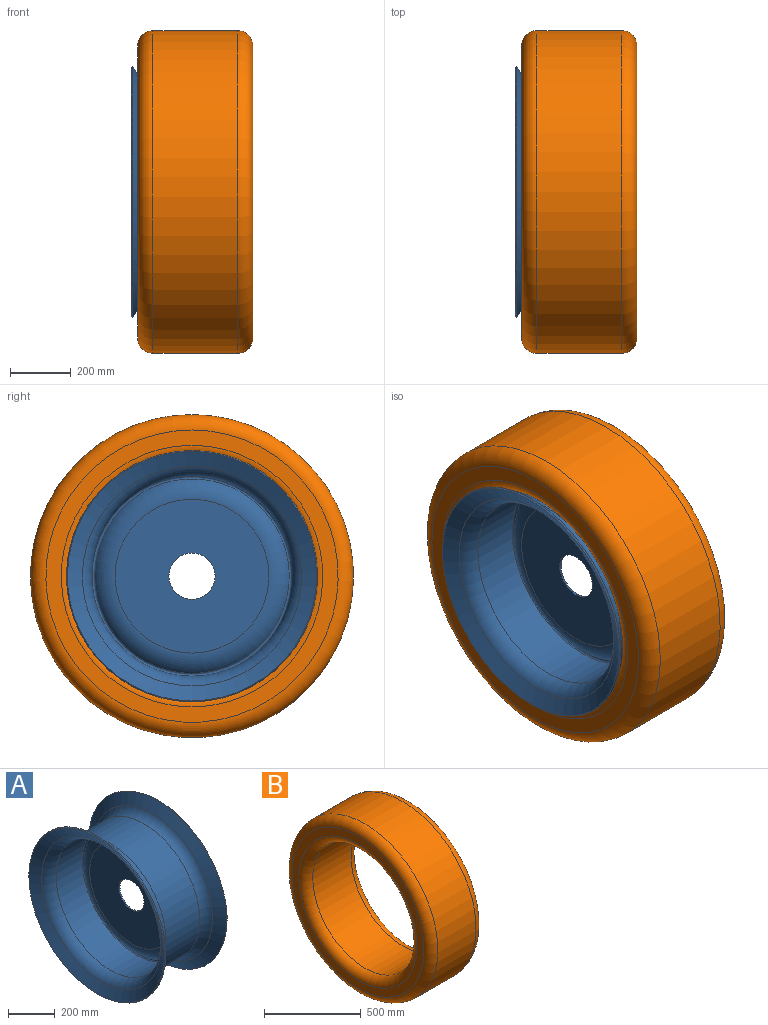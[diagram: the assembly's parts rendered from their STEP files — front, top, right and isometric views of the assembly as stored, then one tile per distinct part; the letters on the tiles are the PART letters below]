
ASSEMBLY  parts=2 mates=1
PART A: 19 faces, bbox 376.3x852.3x852.3 mm
  f0: cone r=416.69mm half-angle=30deg, axis (-1,0,0), area 16688.6mm2, adj f6,f11
  f1: cone r=411.48mm half-angle=30deg, axis (1,0,0), area 16480.7mm2, adj f2,f7
  f2: cone r=365.12mm half-angle=60deg, axis (-1,0,0), area 140106.9mm2, adj f1,f3
  f3: torus R=393.7mm, axis (1,0,0), area 130271.5mm2, adj f2,f4
  f4: cylinder r=336.55mm len=673.1mm, axis (1,0,0), area 435770.6mm2, adj f3,f5
  f5: torus R=393.7mm, axis (1,0,0), area 130271.5mm2, adj f4,f6
  f6: cone r=419.87mm half-angle=60deg, axis (1,0,0), area 155881.4mm2, adj f0,f5
  f7: cone r=361.95mm half-angle=60deg, axis (-1,0,0), area 138966mm2, adj f1,f8
  f8: torus R=393.7mm, axis (1,0,0), area 142552mm2, adj f7,f9
  f9: cylinder r=330.2mm len=660.4mm, axis (1,0,0), area 331161.5mm2, adj f8,f18
  f10: torus R=393.7mm, axis (1,0,0), area 132712.7mm2, adj f11,f13
  f11: cone r=416.69mm half-angle=60deg, axis (1,0,0), area 154620.4mm2, adj f0,f10
  f12: torus R=254mm, axis (1,0,0), area 142547.4mm2, adj f15,f18
  f13: plane 660.75x660.75mm, normal (1,0,0), area 367.2mm2, adj f10,f16
  f14: cylinder r=76.2mm len=152.4mm, axis (-1,0,0), area 3040.2mm2, adj f15,f17
  f15: plane 508x508mm, normal (-1,0,0), area 184441.5mm2, adj f12,f14
  f16: torus R=254mm, axis (1,0,0), area 227507.2mm2, adj f13,f17
  f17: plane 508x508mm, normal (1,0,0), area 184441.5mm2, adj f14,f16
  f18: torus R=325.12mm, axis (1,0,0), area 26221.5mm2, adj f9,f12
PART B: 8 faces, bbox 381x1154.7x1154.7 mm
  f0: cylinder r=381mm len=762mm, axis (-1,0,0), area 668853.9mm2, adj f1,f7
  f1: torus R=431.8mm, axis (-1,0,0), area 200279.5mm2, adj f0,f2
  f2: plane 965.2x965.2mm, normal (1,0,0), area 145931.8mm2, adj f1,f3
  f3: torus R=482.6mm, axis (-1,0,0), area 258178.7mm2, adj f2,f4
  f4: cylinder r=533.4mm len=1066.8mm, axis (-1,0,0), area 936395.4mm2, adj f3,f5
  f5: torus R=482.6mm, axis (-1,0,0), area 258178.7mm2, adj f4,f6
  f6: plane 965.2x965.2mm, normal (-1,0,0), area 145931.8mm2, adj f5,f7
  f7: torus R=431.8mm, axis (-1,0,0), area 200279.5mm2, adj f0,f6
PLACE A t=(-869.38,-123.75,21.16)mm fixed
PLACE B t=(-844.15,-123.75,21.16)mm
MATE fastened B.f0 <-> A.f0  axis (-1,0,0) through (-700.98,-123.75,21.16)mm
